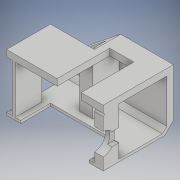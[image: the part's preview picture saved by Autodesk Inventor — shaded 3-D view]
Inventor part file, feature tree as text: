
AUTODESK INVENTOR PART (.ipt)
format: ipt  version: 2018 (Build 220112000, 112)  size: 244,224 bytes
history: native  units: in
note: dims shown in document units (in); Inventor stores cm internally (conversion verified against a paired STEP export)
features: extrude x11, sketch x11
ambient origin geometry x8: Origin, YZ Plane, XZ Plane, XY Plane, X Axis, Y Axis, Z Axis, Center Point
bodies: Solid1 (feature_tree)
feature tree (22):
  extrude  "Extrusion1"  Depth=2.5591in
  extrude  "Extrusion2"  Depth=0.4921in
  sketch  "Sketch3"  dims[d5=0.2953in d6=0.1181in]
  extrude  "Extrusion4"  Depth=0.1181in
  extrude  "Extrusion5"  Depth=0.2953in
  sketch  "Sketch7"  dims[d11=4.3307in d12=0.0in d13=3.937in]
  extrude  "Extrusion6"  Depth=0.3937in
  extrude  "Extrusion7"  Depth=3.937in
  extrude  "Extrusion8"  Depth=1.1811in TaperAngle=0.0deg
  extrude  "Extrusion9"  Depth=0.6299in
  extrude  "Extrusion10"  Depth=3.0709in
  extrude  "Extrusion11"  Depth=1.1811in
  extrude  "Extrusion12"  TaperAngle=0.0deg  [1 undecoded]
  sketch  "Sketch1"  dims[d0=3.1496in d1=2.5591in]
  sketch  "Sketch2"  dims[d3=0.5512in d4=0.4921in]
  sketch  "Sketch4"  dims[d7=0.689in d8=0.2953in]
  sketch  "Sketch5"  dims[d9=0.3937in d10=0.3937in]
  sketch  "Sketch8"  dims[d14=2.1457in d15=1.1811in d16=0.0in]
  sketch  "Sketch9"  dims[d22=1.3386in d23=0.6299in]
  sketch  "Sketch10"  dims[d24=0.6299in d25=3.0709in]
  sketch  "Sketch11"  dims[d26=1.1811in d27=0.0in d28=0.7087in]
  sketch  "Sketch12"  dims[d29=0.0591in d30=0.0in d31=0.0591in d32=1.1811in d33=0.0in d39=1.5748in d40=0.9843in d41=1.9685in d43=0.1969in d44=0.1969in d45=0.1969in d46=1.1811in d47=0.0in d48=0.3937in d49=0.3937in d50=0.1969in d51=0.1969in d52=3.937in d53=0.0in d54=1.1811in d55=0.0in d56=0.5906in d57=0.9843in d58=1.1811in d59=0.0in d60=1.1811in d61=0.0in d62=0.1378in d63=1.1811in d64=0.3937in d65=1.1811in d66=0.0in d67=1.0827in d68=2.3622in d69=0.7874in d70=0.2953in d71=0.3937in d72=0.0in]
note: 1 required parameter value undecoded (feature->parameter linkage not recoverable at this tier; creation-order binding heuristic only, values carry confidence <= 0.55)
